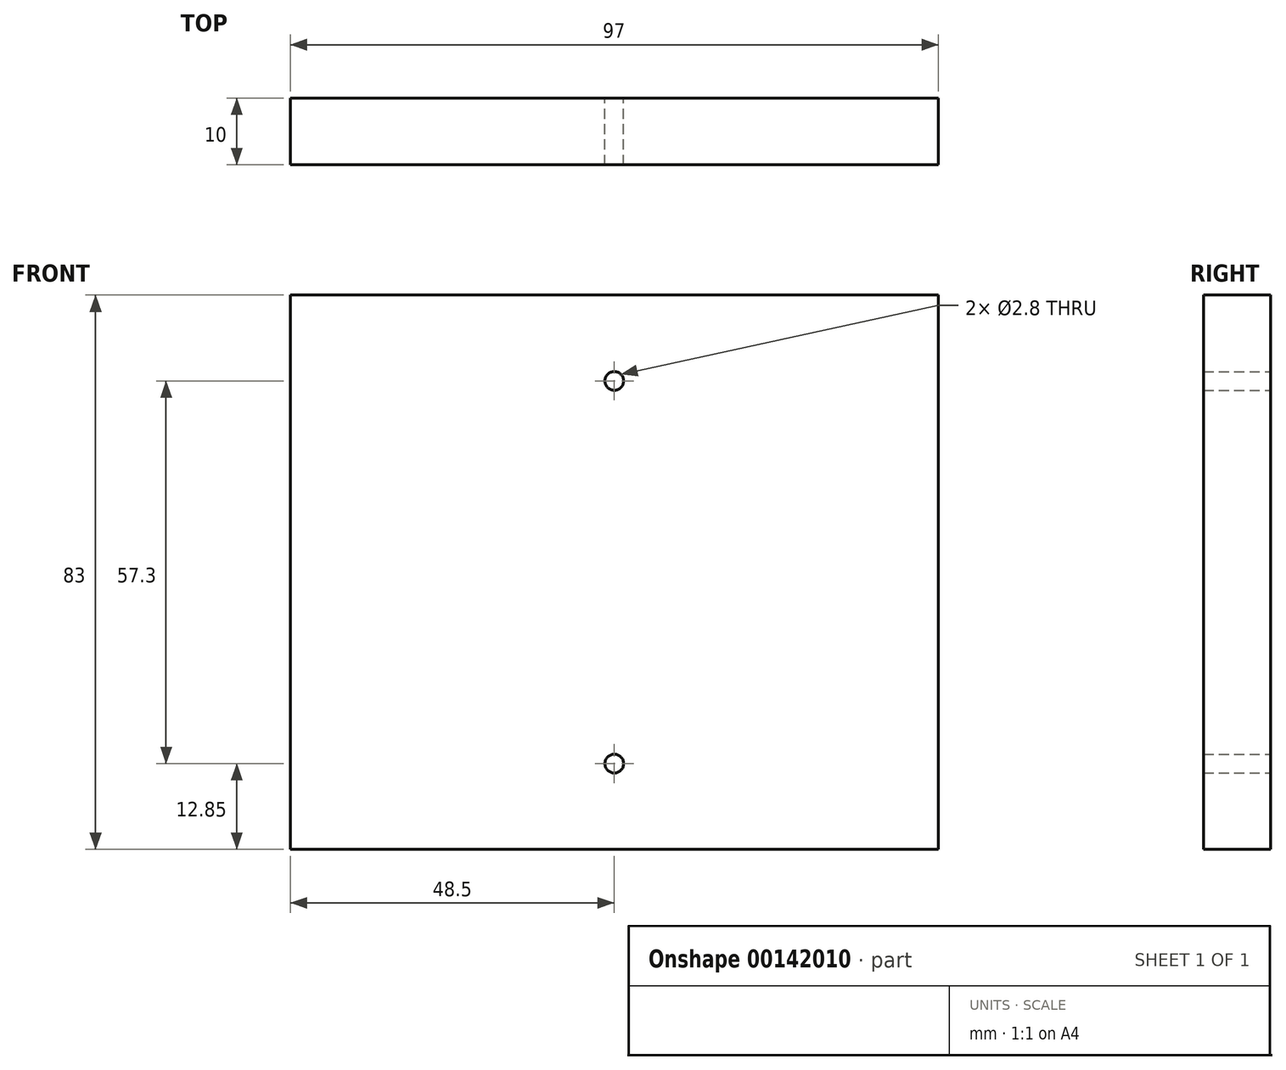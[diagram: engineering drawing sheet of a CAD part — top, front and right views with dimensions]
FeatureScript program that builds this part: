
annotation { "Feature Type Name" : "Feature", "Feature Type Description" : "" }
export const myFeature = defineFeature(function(context is Context, id is Id, definition is map)
    precondition{}
    {
        {
            var Q0;
            Q0=qCreatedBy(makeId("Front.planeOp"),FACE);
            var sketch = newSketch(context, id + "F0", { "sketchPlane" : qUnion([Q0])});
            skLineSegment(sketch, "E0.bottom", {"start": v(48.5, 41.5) * mm, "end": v(-48.5, 41.5) * mm});
            skLineSegment(sketch, "E0.top", {"start": v(48.5, -41.5) * mm, "end": v(-48.5, -41.5) * mm});
            skLineSegment(sketch, "E0.left", {"start": v(48.5, 41.5) * mm, "end": v(48.5, -41.5) * mm});
            skLineSegment(sketch, "E0.right", {"start": v(-48.5, 41.5) * mm, "end": v(-48.5, -41.5) * mm});
            skPoint(sketch, "E0.middle", {"position": v(0, 0) * mm});
            skPoint(sketch, "E1", {"position": v(0, 28.65) * mm});
            skPoint(sketch, "E2", {"position": v(0, -28.65) * mm});
            skCircle(sketch, "E3", {"center": v(0, 28.65) * mm, "radius": 1.4 * mm});
            skCircle(sketch, "E4", {"center": v(0, -28.65) * mm, "radius": 1.4 * mm});
            skPoint(sketch, "E5", {"position": v(0, -27.25) * mm});
            skPoint(sketch, "E6", {"position": v(0, 27.25) * mm});
            skLineSegment(sketch, "E7", {"start": v(-48.5, 0) * mm, "end": v(48.5, 0) * mm, "construction": true});
            skSolve(sketch);
        }
        {
            var Q0;
            Q0 = qSketchRegion(id + "F0", true);
            extrude(context, id + "F1", {"entities" : qUnion([Q0]), "depth" : 10 * mm});
        }
    });
